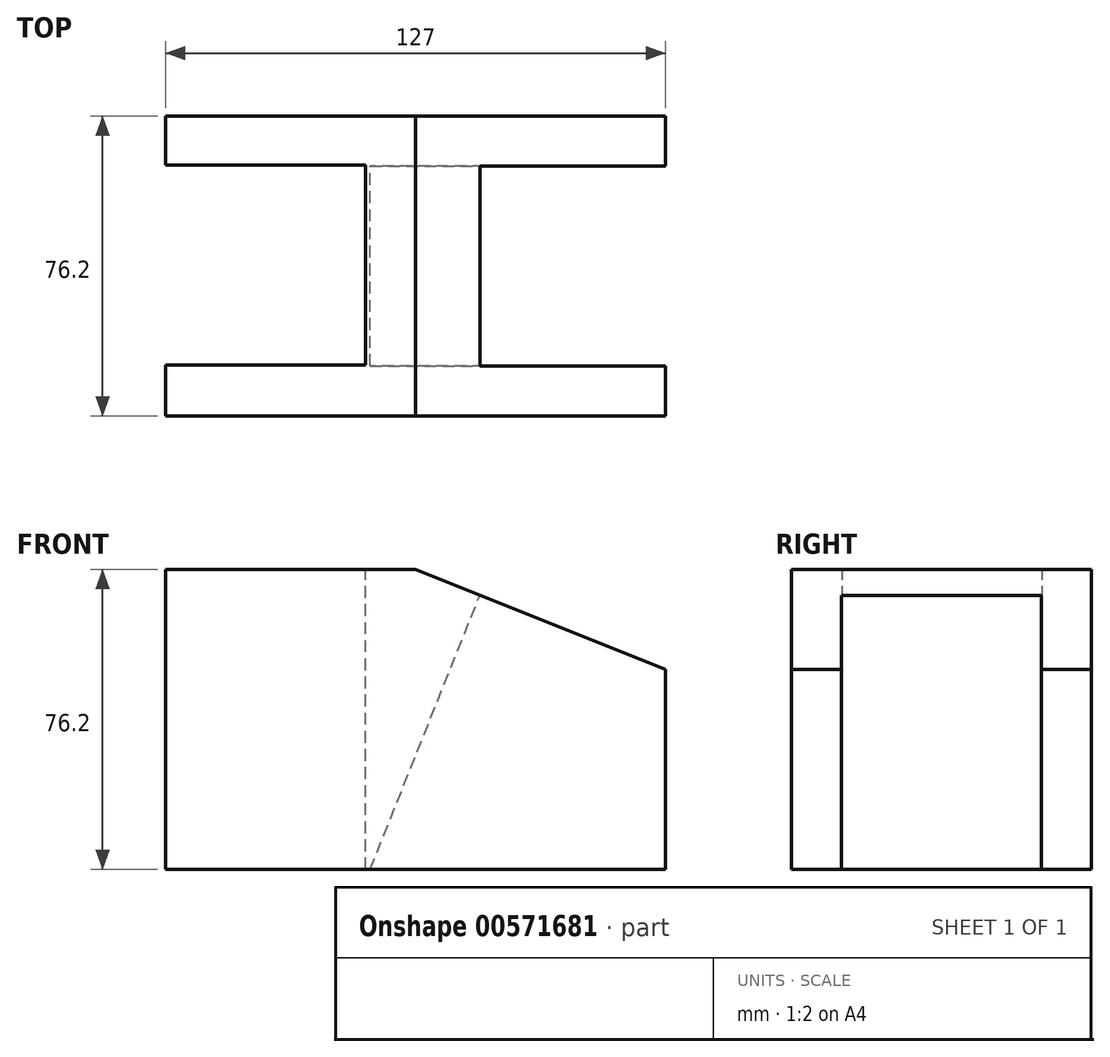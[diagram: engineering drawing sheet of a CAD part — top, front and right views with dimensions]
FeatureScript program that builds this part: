
annotation { "Feature Type Name" : "Feature", "Feature Type Description" : "" }
export const myFeature = defineFeature(function(context is Context, id is Id, definition is map)
    precondition{}
    {
        {
            var Q0;
            Q0=qCreatedBy(makeId("Front.planeOp"),FACE);
            var sketch = newSketch(context, id + "F0", { "sketchPlane" : qUnion([Q0])});
            skLineSegment(sketch, "E0", {"start": v(-79.54, -13.26) * mm, "end": v(-79.54, 62.94) * mm});
            skLineSegment(sketch, "E1", {"start": v(-79.54, 62.94) * mm, "end": v(-16.04, 62.94) * mm});
            skLineSegment(sketch, "E2", {"start": v(-79.54, -13.26) * mm, "end": v(47.46, -13.26) * mm});
            skLineSegment(sketch, "E3", {"start": v(47.46, -13.26) * mm, "end": v(47.46, 37.54) * mm});
            skLineSegment(sketch, "E4", {"start": v(-16.04, 62.94) * mm, "end": v(47.46, 37.54) * mm});
            skSolve(sketch);
        }
        {
            var Q0;
            Q0 = qSketchRegion(id + "F0", true);
            extrude(context, id + "F1", {"entities" : qUnion([Q0]), "depth" : 76.2 * mm, "offsetDistance" : 25.4 * mm});
        }
        {
            var Q0;
            Q0=makeQuery(id+"F1.opExtrude","SWEPT_FACE",FACE,{"disambiguationData":[OSD([sQuery(id+"F0.wireOp",EDGE,"E4")])]});
            var sketch = newSketch(context, id + "F2", { "sketchPlane" : qUnion([Q0])});
            skLineSegment(sketch, "E5.bottom", {"start": v(30.12, -63.5) * mm, "end": v(-20.68, -63.5) * mm});
            skLineSegment(sketch, "E5.top", {"start": v(30.12, -12.7) * mm, "end": v(-20.68, -12.7) * mm});
            skLineSegment(sketch, "E5.left", {"start": v(30.12, -63.5) * mm, "end": v(30.12, -12.7) * mm});
            skLineSegment(sketch, "E5.right", {"start": v(-20.68, -63.5) * mm, "end": v(-20.68, -12.7) * mm});
            skPoint(sketch, "E6.end.orphan", {"position": v(30.12, -12.7) * mm});
            skSolve(sketch);
        }
        {
            var Q0;
            Q0 = qSketchRegion(id + "F2", true);
            extrude(context, id + "F3", {"entities" : qUnion([Q0]), "operationType" : NewBodyOperationType.REMOVE, "oppositeDirection" : true, "depth" : 94.23 * mm, "offsetDistance" : 25.4 * mm});
        }
        {
            var Q0;
            Q0=makeQuery(id+"F3.boolean.opBoolean","COPY",FACE,{"derivedFrom":makeQuery(id+"F3.opExtrude","SWEPT_FACE",FACE,{"disambiguationData":[OSD([sQuery(id+"F2.wireOp",EDGE,"E5.left")])]})});
            var sketch = newSketch(context, id + "F4", { "sketchPlane" : qUnion([Q0])});
            skLineSegment(sketch, "E7.bottom", {"start": v(63.5, -2.23) * mm, "end": v(12.7, -2.23) * mm});
            skLineSegment(sketch, "E7.top", {"start": v(63.5, 132.7) * mm, "end": v(12.7, 132.7) * mm});
            skLineSegment(sketch, "E7.left", {"start": v(63.5, -2.23) * mm, "end": v(63.5, 132.7) * mm});
            skLineSegment(sketch, "E7.right", {"start": v(12.7, -2.23) * mm, "end": v(12.7, 132.7) * mm});
            skSolve(sketch);
        }
        {
            var Q0;
            Q0 = qSketchRegion(id + "F4", true);
            extrude(context, id + "F5", {"entities" : qUnion([Q0]), "operationType" : NewBodyOperationType.REMOVE, "oppositeDirection" : true, "depth" : 41.66 * mm, "offsetDistance" : 25.4 * mm});
        }
        {
            var Q0;
            Q0=makeQuery(id+"F1.opExtrude","SWEPT_FACE",FACE,{"disambiguationData":[OSD([sQuery(id+"F0.wireOp",EDGE,"E1")])]});
            var sketch = newSketch(context, id + "F6", { "sketchPlane" : qUnion([Q0])});
            skLineSegment(sketch, "E8.bottom", {"start": v(-79.54, -63.27) * mm, "end": v(-28.74, -63.27) * mm});
            skLineSegment(sketch, "E8.top", {"start": v(-79.54, -12.47) * mm, "end": v(-28.74, -12.47) * mm});
            skLineSegment(sketch, "E8.left", {"start": v(-79.54, -63.27) * mm, "end": v(-79.54, -12.47) * mm});
            skLineSegment(sketch, "E8.right", {"start": v(-28.74, -63.27) * mm, "end": v(-28.74, -12.47) * mm});
            skSolve(sketch);
        }
        {
            var Q0;
            Q0 = qSketchRegion(id + "F6", true);
            extrude(context, id + "F7", {"entities" : qUnion([Q0]), "operationType" : NewBodyOperationType.REMOVE, "oppositeDirection" : true, "depth" : 88.14 * mm, "offsetDistance" : 25.4 * mm});
        }
    });
